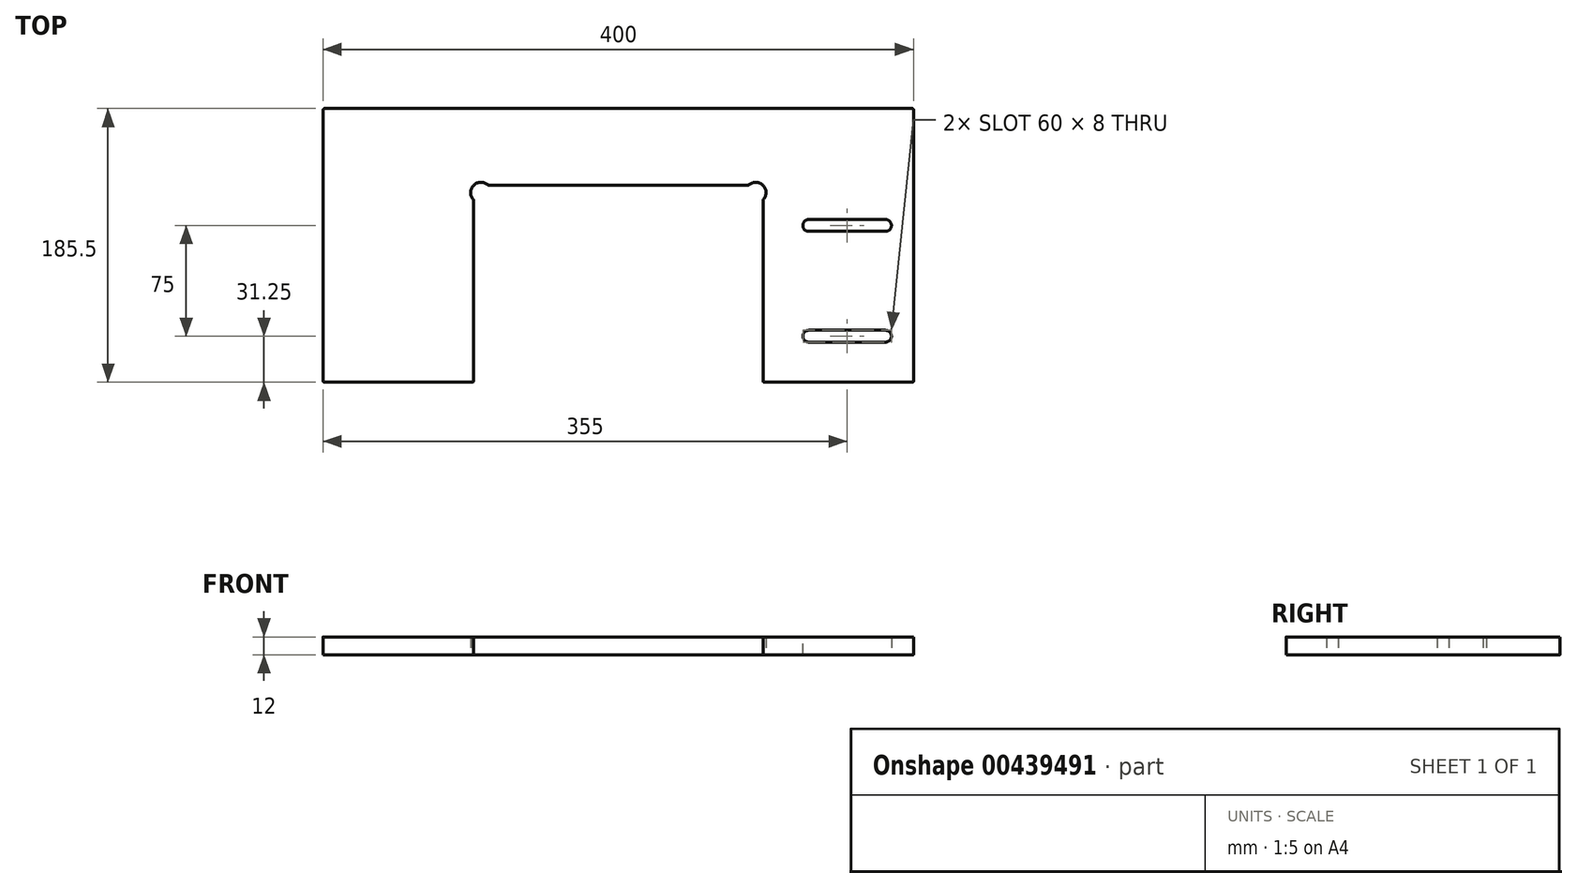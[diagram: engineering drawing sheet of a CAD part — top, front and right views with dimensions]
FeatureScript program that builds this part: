
annotation { "Feature Type Name" : "Feature", "Feature Type Description" : "" }
export const myFeature = defineFeature(function(context is Context, id is Id, definition is map)
    precondition{}
    {
        {
            var Q0;
            Q0=qCreatedBy(makeId("Top.planeOp"),FACE);
            var sketch = newSketch(context, id + "F0", { "sketchPlane" : qUnion([Q0])});
            skLineSegment(sketch, "E0", {"start": v(-200, 0) * mm, "end": v(200, 0) * mm});
            skLineSegment(sketch, "E1", {"start": v(200, 0) * mm, "end": v(200, -229) * mm});
            skLineSegment(sketch, "E2", {"start": v(200, -229) * mm, "end": v(98, -229) * mm});
            skLineSegment(sketch, "E3", {"start": v(98, -229) * mm, "end": v(98, -61.9) * mm});
            skLineSegment(sketch, "E4", {"start": v(88.1, -52) * mm, "end": v(-88.1, -52) * mm});
            skLineSegment(sketch, "E5", {"start": v(-98, -61.9) * mm, "end": v(-98, -229) * mm});
            skLineSegment(sketch, "E6", {"start": v(-98, -229) * mm, "end": v(-200, -229) * mm});
            skLineSegment(sketch, "E7", {"start": v(-200, -229) * mm, "end": v(-200, 0) * mm});
            skArc(sketch, "E8", {"start": v(98, -61.9) * mm, "mid": v(98, -52) * mm, "end": v(88.1, -52) * mm});
            skArc(sketch, "E9", {"start": v(-88.1, -52) * mm, "mid": v(-98, -52) * mm, "end": v(-98, -61.9) * mm});
            skLineSegment(sketch, "E10", {"start": v(-98, -61.9) * mm, "end": v(-98, -52) * mm, "construction": true});
            skLineSegment(sketch, "E11", {"start": v(-98, -52) * mm, "end": v(-88.1, -52) * mm, "construction": true});
            skLineSegment(sketch, "E12", {"start": v(88.1, -52) * mm, "end": v(98, -52) * mm, "construction": true});
            skLineSegment(sketch, "E13", {"start": v(98, -52) * mm, "end": v(98, -61.9) * mm, "construction": true});
            skLineSegment(sketch, "E14", {"start": v(-98, -185.5) * mm, "end": v(-200, -185.5) * mm});
            skLineSegment(sketch, "E15", {"start": v(98, -185.5) * mm, "end": v(200, -185.5) * mm});
            skLineSegment(sketch, "E16", {"start": v(155, -185.5) * mm, "end": v(155, -79.25) * mm, "construction": true});
            skLineSegment(sketch, "E17.bottom", {"start": v(125, -150.25) * mm, "end": v(185, -150.25) * mm});
            skLineSegment(sketch, "E17.top", {"start": v(125, -158.25) * mm, "end": v(185, -158.25) * mm});
            skLineSegment(sketch, "E17.left", {"start": v(125, -150.25) * mm, "end": v(125, -158.25) * mm});
            skLineSegment(sketch, "E17.right", {"start": v(185, -150.25) * mm, "end": v(185, -158.25) * mm});
            skPoint(sketch, "E17.middle", {"position": v(155, -154.25) * mm});
            skLineSegment(sketch, "E18.bottom", {"start": v(125, -75.25) * mm, "end": v(185, -75.25) * mm});
            skLineSegment(sketch, "E18.top", {"start": v(125, -83.25) * mm, "end": v(185, -83.25) * mm});
            skLineSegment(sketch, "E18.left", {"start": v(125, -75.25) * mm, "end": v(125, -83.25) * mm});
            skLineSegment(sketch, "E18.right", {"start": v(185, -75.25) * mm, "end": v(185, -83.25) * mm});
            skPoint(sketch, "E18.middle", {"position": v(155, -79.25) * mm});
            skSolve(sketch);
        }
        {
            var Q0;
            {var subQ1=sQuery(id+"F0.wireOp",EDGE,"E0");Q0=makeQuery(id+"F0.imprint","IMPRINT",FACE,{"disambiguationData":[TD([[makeQuery(id+"F0.imprint","IMPRINT",EDGE,{"derivedFrom":subQ1}),-1.0]])]});}
            extrude(context, id + "F1", {"entities" : qUnion([Q0]), "depth" : 12 * mm, "offsetDistance" : 25 * mm});
        }
        {
            var Q0;
            Q0=makeQuery(id+"F1.opExtrude","SWEPT_EDGE",EDGE,{"disambiguationData":[OSD([sQuery(id+"F0.wireOp",EDGE,"E5"),sQuery(id+"F0.wireOp",EDGE,"E6")])]});
            var Q1;
            Q1=makeQuery(id+"F1.opExtrude","SWEPT_EDGE",EDGE,{"disambiguationData":[OSD([sQuery(id+"F0.wireOp",EDGE,"E5"),sQuery(id+"F0.wireOp",EDGE,"E9")])]});
            var Q2;
            Q2=makeQuery(id+"F1.opExtrude","SWEPT_EDGE",EDGE,{"disambiguationData":[OSD([sQuery(id+"F0.wireOp",EDGE,"E4"),sQuery(id+"F0.wireOp",EDGE,"E9")])]});
            var Q3;
            Q3=makeQuery(id+"F1.opExtrude","SWEPT_EDGE",EDGE,{"disambiguationData":[OSD([sQuery(id+"F0.wireOp",EDGE,"E4"),sQuery(id+"F0.wireOp",EDGE,"E8")])]});
            var Q4;
            Q4=makeQuery(id+"F1.opExtrude","SWEPT_EDGE",EDGE,{"disambiguationData":[OSD([sQuery(id+"F0.wireOp",EDGE,"E3"),sQuery(id+"F0.wireOp",EDGE,"E8")])]});
            var Q5;
            Q5=makeQuery(id+"F1.opExtrude","SWEPT_EDGE",EDGE,{"disambiguationData":[OSD([sQuery(id+"F0.wireOp",EDGE,"E2"),sQuery(id+"F0.wireOp",EDGE,"E3")])]});
            var Q6;
            Q6=makeQuery(id+"F1.opExtrude","SWEPT_EDGE",EDGE,{"disambiguationData":[OSD([sQuery(id+"F0.wireOp",EDGE,"E1"),sQuery(id+"F0.wireOp",EDGE,"E2")])]});
            var Q7;
            Q7=makeQuery(id+"F1.opExtrude","SWEPT_EDGE",EDGE,{"disambiguationData":[OSD([sQuery(id+"F0.wireOp",EDGE,"E0"),sQuery(id+"F0.wireOp",EDGE,"E1")])]});
            var Q8;
            Q8=makeQuery(id+"F1.opExtrude","SWEPT_EDGE",EDGE,{"disambiguationData":[OSD([sQuery(id+"F0.wireOp",EDGE,"E0"),sQuery(id+"F0.wireOp",EDGE,"E7")])]});
            var Q9;
            Q9=makeQuery(id+"F1.opExtrude","SWEPT_EDGE",EDGE,{"disambiguationData":[OSD([sQuery(id+"F0.wireOp",EDGE,"E6"),sQuery(id+"F0.wireOp",EDGE,"E7")])]});
            fillet(context, id + "F2", {"entities" : qUnion([Q0, Q1, Q2, Q3, Q4, Q5, Q6, Q7, Q8, Q9]), "radius" : 1 * mm, "tangentPropagation" : true, "allowEdgeOverflow" : false});
        }
        {
            var Q0;
            Q0=makeQuery(id+"F1.opExtrude","SWEPT_EDGE",EDGE,{"disambiguationData":[OSD([sQuery(id+"F0.wireOp",EDGE,"E17.top"),sQuery(id+"F0.wireOp",EDGE,"E17.left")])]});
            var Q1;
            Q1=makeQuery(id+"F1.opExtrude","SWEPT_EDGE",EDGE,{"disambiguationData":[OSD([sQuery(id+"F0.wireOp",EDGE,"E17.bottom"),sQuery(id+"F0.wireOp",EDGE,"E17.left")])]});
            var Q2;
            Q2=makeQuery(id+"F1.opExtrude","SWEPT_EDGE",EDGE,{"disambiguationData":[OSD([sQuery(id+"F0.wireOp",EDGE,"E17.top"),sQuery(id+"F0.wireOp",EDGE,"E17.right")])]});
            var Q3;
            Q3=makeQuery(id+"F1.opExtrude","SWEPT_EDGE",EDGE,{"disambiguationData":[OSD([sQuery(id+"F0.wireOp",EDGE,"E17.bottom"),sQuery(id+"F0.wireOp",EDGE,"E17.right")])]});
            var Q4;
            Q4=makeQuery(id+"F1.opExtrude","SWEPT_EDGE",EDGE,{"disambiguationData":[OSD([sQuery(id+"F0.wireOp",EDGE,"E18.top"),sQuery(id+"F0.wireOp",EDGE,"E18.left")])]});
            var Q5;
            Q5=makeQuery(id+"F1.opExtrude","SWEPT_EDGE",EDGE,{"disambiguationData":[OSD([sQuery(id+"F0.wireOp",EDGE,"E18.bottom"),sQuery(id+"F0.wireOp",EDGE,"E18.left")])]});
            var Q6;
            Q6=makeQuery(id+"F1.opExtrude","SWEPT_EDGE",EDGE,{"disambiguationData":[OSD([sQuery(id+"F0.wireOp",EDGE,"E18.top"),sQuery(id+"F0.wireOp",EDGE,"E18.right")])]});
            var Q7;
            Q7=makeQuery(id+"F1.opExtrude","SWEPT_EDGE",EDGE,{"disambiguationData":[OSD([sQuery(id+"F0.wireOp",EDGE,"E18.bottom"),sQuery(id+"F0.wireOp",EDGE,"E18.right")])]});
            fillet(context, id + "F3", {"entities" : qUnion([Q0, Q1, Q2, Q3, Q4, Q5, Q6, Q7]), "tangentPropagation" : true, "radius" : 4 * mm, "defaultsChanged" : false, "vertexSettings" : [], "allowEdgeOverflow" : false});
        }
    });
